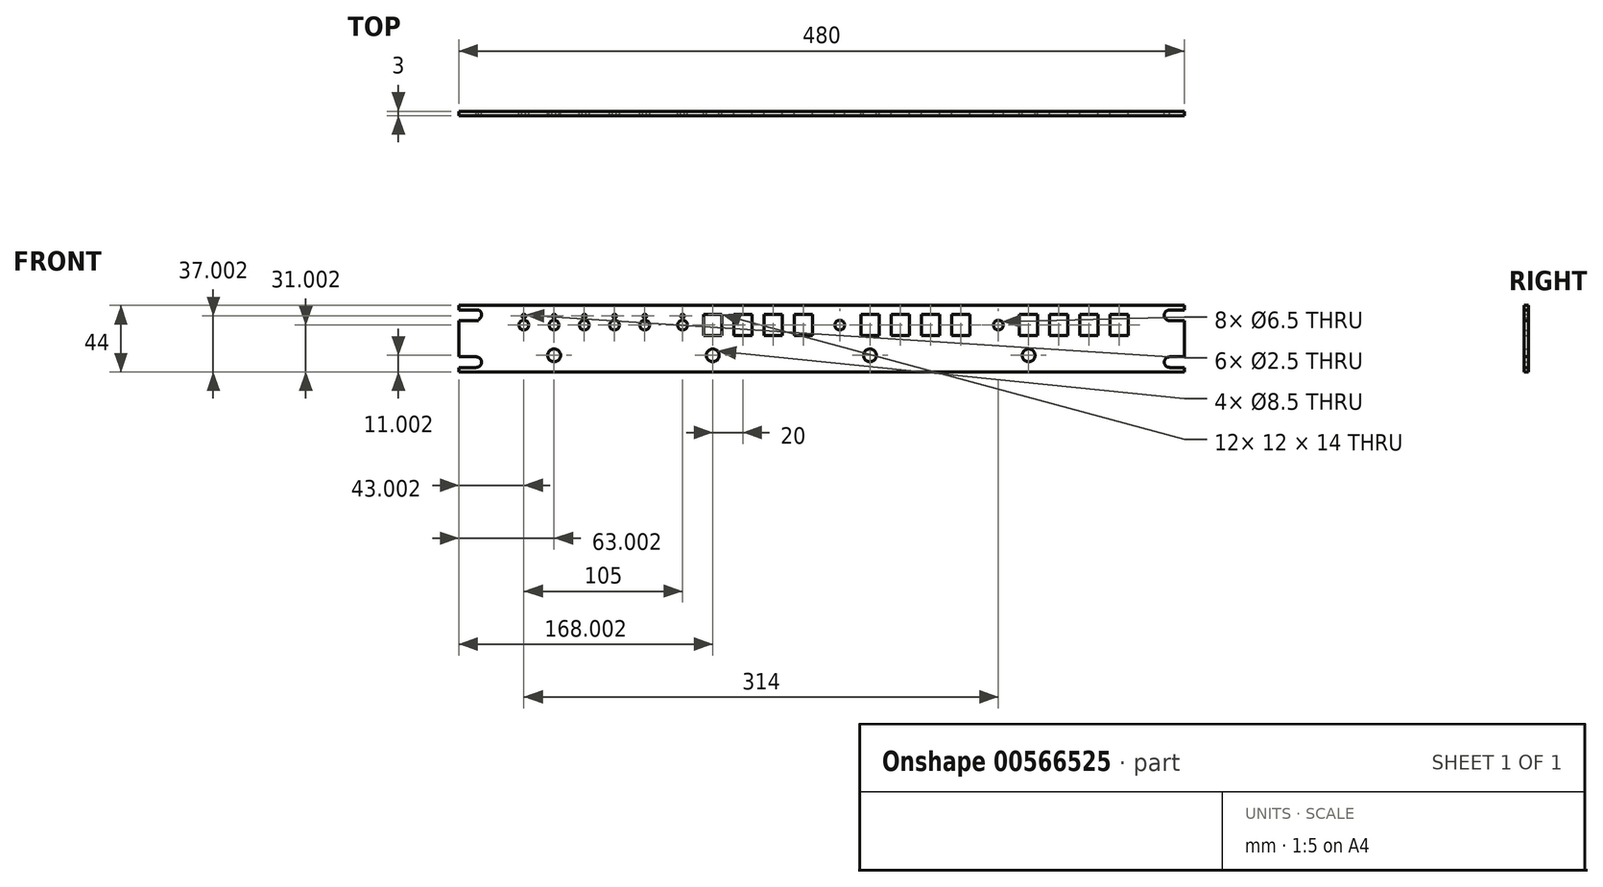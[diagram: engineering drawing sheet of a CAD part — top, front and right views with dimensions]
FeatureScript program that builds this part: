
annotation { "Feature Type Name" : "Feature", "Feature Type Description" : "" }
export const myFeature = defineFeature(function(context is Context, id is Id, definition is map)
    precondition{}
    {
        {
            var Q0;
            Q0=qCreatedBy(makeId("Front.planeOp"),FACE);
            var sketch = newSketch(context, id + "F0", { "sketchPlane" : qUnion([Q0])});
            skLineSegment(sketch, "E0.bottom", {"start": v(-244.03, -52.88) * mm, "end": v(235.97, -52.88) * mm});
            skLineSegment(sketch, "E0.top", {"start": v(-244.03, -96.88) * mm, "end": v(235.97, -96.88) * mm});
            skLineSegment(sketch, "E0.left", {"start": v(-244.03, -52.88) * mm, "end": v(-244.03, -55.88) * mm});
            skLineSegment(sketch, "E0.right", {"start": v(235.97, -52.88) * mm, "end": v(235.97, -55.88) * mm});
            skLineSegment(sketch, "E1.bottom", {"start": v(-207.03, -58.88) * mm, "end": v(-195.03, -58.88) * mm});
            skLineSegment(sketch, "E1.top", {"start": v(-207.03, -72.88) * mm, "end": v(-195.03, -72.88) * mm});
            skLineSegment(sketch, "E1.left", {"start": v(-207.03, -58.88) * mm, "end": v(-207.03, -72.88) * mm});
            skLineSegment(sketch, "E1.right", {"start": v(-195.03, -58.88) * mm, "end": v(-195.03, -72.88) * mm});
            skLineSegment(sketch, "E2.bottom", {"start": v(-187.03, -58.88) * mm, "end": v(-175.03, -58.88) * mm});
            skLineSegment(sketch, "E2.top", {"start": v(-187.03, -72.88) * mm, "end": v(-175.03, -72.88) * mm});
            skLineSegment(sketch, "E2.left", {"start": v(-187.03, -58.88) * mm, "end": v(-187.03, -72.88) * mm});
            skLineSegment(sketch, "E2.right", {"start": v(-175.03, -58.88) * mm, "end": v(-175.03, -72.88) * mm});
            skLineSegment(sketch, "E3.bottom", {"start": v(-167.03, -58.88) * mm, "end": v(-155.03, -58.88) * mm});
            skLineSegment(sketch, "E3.top", {"start": v(-167.03, -72.88) * mm, "end": v(-155.03, -72.88) * mm});
            skLineSegment(sketch, "E3.left", {"start": v(-167.03, -58.88) * mm, "end": v(-167.03, -72.88) * mm});
            skLineSegment(sketch, "E3.right", {"start": v(-155.03, -58.88) * mm, "end": v(-155.03, -72.88) * mm});
            skLineSegment(sketch, "E4.bottom", {"start": v(-147.03, -58.88) * mm, "end": v(-135.03, -58.88) * mm});
            skLineSegment(sketch, "E4.top", {"start": v(-147.03, -72.88) * mm, "end": v(-135.03, -72.88) * mm});
            skLineSegment(sketch, "E4.left", {"start": v(-147.03, -58.88) * mm, "end": v(-147.03, -72.88) * mm});
            skLineSegment(sketch, "E4.right", {"start": v(-135.03, -58.88) * mm, "end": v(-135.03, -72.88) * mm});
            skLineSegment(sketch, "E5.bottom", {"start": v(-127.03, -58.88) * mm, "end": v(-115.03, -58.88) * mm});
            skLineSegment(sketch, "E5.top", {"start": v(-127.03, -72.88) * mm, "end": v(-115.03, -72.88) * mm});
            skLineSegment(sketch, "E5.left", {"start": v(-127.03, -58.88) * mm, "end": v(-127.03, -72.88) * mm});
            skLineSegment(sketch, "E5.right", {"start": v(-115.03, -58.88) * mm, "end": v(-115.03, -72.88) * mm});
            skCircle(sketch, "E6", {"center": v(-181.03, -85.88) * mm, "radius": 4.25 * mm});
            skCircle(sketch, "E7", {"center": v(-201.03, -65.88) * mm, "radius": 3.25 * mm});
            skLineSegment(sketch, "E8.bottom", {"start": v(-102.03, -58.88) * mm, "end": v(-90.03, -58.88) * mm});
            skLineSegment(sketch, "E8.top", {"start": v(-102.03, -72.88) * mm, "end": v(-90.03, -72.88) * mm});
            skLineSegment(sketch, "E8.left", {"start": v(-102.03, -58.88) * mm, "end": v(-102.03, -72.88) * mm});
            skLineSegment(sketch, "E8.right", {"start": v(-90.03, -58.88) * mm, "end": v(-90.03, -72.88) * mm});
            skLineSegment(sketch, "E9.bottom", {"start": v(-82.03, -58.88) * mm, "end": v(-70.03, -58.88) * mm});
            skLineSegment(sketch, "E9.top", {"start": v(-82.03, -72.88) * mm, "end": v(-70.03, -72.88) * mm});
            skLineSegment(sketch, "E9.left", {"start": v(-82.03, -58.88) * mm, "end": v(-82.03, -72.88) * mm});
            skLineSegment(sketch, "E9.right", {"start": v(-70.03, -58.88) * mm, "end": v(-70.03, -72.88) * mm});
            skLineSegment(sketch, "E10.bottom", {"start": v(-62.03, -58.88) * mm, "end": v(-50.03, -58.88) * mm});
            skLineSegment(sketch, "E10.top", {"start": v(-62.03, -72.88) * mm, "end": v(-50.03, -72.88) * mm});
            skLineSegment(sketch, "E10.left", {"start": v(-62.03, -58.88) * mm, "end": v(-62.03, -72.88) * mm});
            skLineSegment(sketch, "E10.right", {"start": v(-50.03, -58.88) * mm, "end": v(-50.03, -72.88) * mm});
            skLineSegment(sketch, "E11.bottom", {"start": v(-42.03, -58.88) * mm, "end": v(-30.03, -58.88) * mm});
            skLineSegment(sketch, "E11.top", {"start": v(-42.03, -72.88) * mm, "end": v(-30.03, -72.88) * mm});
            skLineSegment(sketch, "E11.left", {"start": v(-42.03, -58.88) * mm, "end": v(-42.03, -72.88) * mm});
            skLineSegment(sketch, "E11.right", {"start": v(-30.03, -58.88) * mm, "end": v(-30.03, -72.88) * mm});
            skLineSegment(sketch, "E12.bottom", {"start": v(-22.03, -58.88) * mm, "end": v(-10.03, -58.88) * mm});
            skLineSegment(sketch, "E12.top", {"start": v(-22.03, -72.88) * mm, "end": v(-10.03, -72.88) * mm});
            skLineSegment(sketch, "E12.left", {"start": v(-22.03, -58.88) * mm, "end": v(-22.03, -72.88) * mm});
            skLineSegment(sketch, "E12.right", {"start": v(-10.03, -58.88) * mm, "end": v(-10.03, -72.88) * mm});
            skCircle(sketch, "E13", {"center": v(-76.03, -85.88) * mm, "radius": 4.25 * mm});
            skCircle(sketch, "E14", {"center": v(-96.03, -65.88) * mm, "radius": 3.25 * mm});
            skLineSegment(sketch, "E15.bottom", {"start": v(1.97, -58.88) * mm, "end": v(13.97, -58.88) * mm});
            skLineSegment(sketch, "E15.top", {"start": v(1.97, -72.88) * mm, "end": v(13.97, -72.88) * mm});
            skLineSegment(sketch, "E15.left", {"start": v(1.97, -58.88) * mm, "end": v(1.97, -72.88) * mm});
            skLineSegment(sketch, "E15.right", {"start": v(13.97, -58.88) * mm, "end": v(13.97, -72.88) * mm});
            skLineSegment(sketch, "E16.bottom", {"start": v(21.97, -58.88) * mm, "end": v(33.97, -58.88) * mm});
            skLineSegment(sketch, "E16.top", {"start": v(21.97, -72.88) * mm, "end": v(33.97, -72.88) * mm});
            skLineSegment(sketch, "E16.left", {"start": v(21.97, -58.88) * mm, "end": v(21.97, -72.88) * mm});
            skLineSegment(sketch, "E16.right", {"start": v(33.97, -58.88) * mm, "end": v(33.97, -72.88) * mm});
            skLineSegment(sketch, "E17.bottom", {"start": v(41.97, -58.88) * mm, "end": v(53.97, -58.88) * mm});
            skLineSegment(sketch, "E17.top", {"start": v(41.97, -72.88) * mm, "end": v(53.97, -72.88) * mm});
            skLineSegment(sketch, "E17.left", {"start": v(41.97, -58.88) * mm, "end": v(41.97, -72.88) * mm});
            skLineSegment(sketch, "E17.right", {"start": v(53.97, -58.88) * mm, "end": v(53.97, -72.88) * mm});
            skLineSegment(sketch, "E18.bottom", {"start": v(61.97, -58.88) * mm, "end": v(73.97, -58.88) * mm});
            skLineSegment(sketch, "E18.top", {"start": v(61.97, -72.88) * mm, "end": v(73.97, -72.88) * mm});
            skLineSegment(sketch, "E18.left", {"start": v(61.97, -58.88) * mm, "end": v(61.97, -72.88) * mm});
            skLineSegment(sketch, "E18.right", {"start": v(73.97, -58.88) * mm, "end": v(73.97, -72.88) * mm});
            skLineSegment(sketch, "E19.bottom", {"start": v(81.97, -58.88) * mm, "end": v(93.97, -58.88) * mm});
            skLineSegment(sketch, "E19.top", {"start": v(81.97, -72.88) * mm, "end": v(93.97, -72.88) * mm});
            skLineSegment(sketch, "E19.left", {"start": v(81.97, -58.88) * mm, "end": v(81.97, -72.88) * mm});
            skLineSegment(sketch, "E19.right", {"start": v(93.97, -58.88) * mm, "end": v(93.97, -72.88) * mm});
            skCircle(sketch, "E20", {"center": v(27.97, -85.88) * mm, "radius": 4.25 * mm});
            skCircle(sketch, "E21", {"center": v(7.97, -65.88) * mm, "radius": 3.25 * mm});
            skLineSegment(sketch, "E22.bottom", {"start": v(106.97, -58.88) * mm, "end": v(118.97, -58.88) * mm});
            skLineSegment(sketch, "E22.top", {"start": v(106.97, -72.88) * mm, "end": v(118.97, -72.88) * mm});
            skLineSegment(sketch, "E22.left", {"start": v(106.97, -58.88) * mm, "end": v(106.97, -72.88) * mm});
            skLineSegment(sketch, "E22.right", {"start": v(118.97, -58.88) * mm, "end": v(118.97, -72.88) * mm});
            skLineSegment(sketch, "E23.bottom", {"start": v(126.97, -58.88) * mm, "end": v(138.97, -58.88) * mm});
            skLineSegment(sketch, "E23.top", {"start": v(126.97, -72.88) * mm, "end": v(138.97, -72.88) * mm});
            skLineSegment(sketch, "E23.left", {"start": v(126.97, -58.88) * mm, "end": v(126.97, -72.88) * mm});
            skLineSegment(sketch, "E23.right", {"start": v(138.97, -58.88) * mm, "end": v(138.97, -72.88) * mm});
            skLineSegment(sketch, "E24.bottom", {"start": v(146.97, -58.88) * mm, "end": v(158.97, -58.88) * mm});
            skLineSegment(sketch, "E24.top", {"start": v(146.97, -72.88) * mm, "end": v(158.97, -72.88) * mm});
            skLineSegment(sketch, "E24.left", {"start": v(146.97, -58.88) * mm, "end": v(146.97, -72.88) * mm});
            skLineSegment(sketch, "E24.right", {"start": v(158.97, -58.88) * mm, "end": v(158.97, -72.88) * mm});
            skLineSegment(sketch, "E25.bottom", {"start": v(166.97, -58.88) * mm, "end": v(178.97, -58.88) * mm});
            skLineSegment(sketch, "E25.top", {"start": v(166.97, -72.88) * mm, "end": v(178.97, -72.88) * mm});
            skLineSegment(sketch, "E25.left", {"start": v(166.97, -58.88) * mm, "end": v(166.97, -72.88) * mm});
            skLineSegment(sketch, "E25.right", {"start": v(178.97, -58.88) * mm, "end": v(178.97, -72.88) * mm});
            skLineSegment(sketch, "E26.bottom", {"start": v(186.97, -58.88) * mm, "end": v(198.97, -58.88) * mm});
            skLineSegment(sketch, "E26.top", {"start": v(186.97, -72.88) * mm, "end": v(198.97, -72.88) * mm});
            skLineSegment(sketch, "E26.left", {"start": v(186.97, -58.88) * mm, "end": v(186.97, -72.88) * mm});
            skLineSegment(sketch, "E26.right", {"start": v(198.97, -58.88) * mm, "end": v(198.97, -72.88) * mm});
            skCircle(sketch, "E27", {"center": v(132.97, -85.88) * mm, "radius": 4.25 * mm});
            skCircle(sketch, "E28", {"center": v(112.97, -65.88) * mm, "radius": 3.25 * mm});
            skArc(sketch, "E29", {"start": v(-230.86, -62.03) * mm, "mid": v(-229.03, -58.95) * mm, "end": v(-230.86, -55.88) * mm});
            skLineSegment(sketch, "E30.bottom", {"start": v(-230.86, -55.88) * mm, "end": v(-244.03, -55.88) * mm});
            skLineSegment(sketch, "E30.top", {"start": v(-230.86, -63.01) * mm, "end": v(-244.03, -63.01) * mm});
            skLineSegment(sketch, "E30.left", {"start": v(-230.86, -62.03) * mm, "end": v(-230.86, -63.01) * mm});
            skLineSegment(sketch, "E31.trimOffspring", {"start": v(-244.03, -63.01) * mm, "end": v(-244.03, -86.88) * mm});
            skArc(sketch, "E32", {"start": v(-232.6, -93.88) * mm, "mid": v(-229.03, -90.38) * mm, "end": v(-232.6, -86.88) * mm});
            skLineSegment(sketch, "E33.bottom", {"start": v(-232.6, -86.88) * mm, "end": v(-244.03, -86.88) * mm});
            skLineSegment(sketch, "E33.top", {"start": v(-232.6, -93.88) * mm, "end": v(-244.03, -93.88) * mm});
            skLineSegment(sketch, "E33.left", {"start": v(-232.6, -93.88) * mm, "end": v(-232.6, -93.88) * mm});
            skLineSegment(sketch, "E34.trimOffspring", {"start": v(-244.03, -93.88) * mm, "end": v(-244.03, -96.88) * mm});
            skLineSegment(sketch, "E35.MirrorCS", {"start": v(226.3, -93.88) * mm, "end": v(226.3, -93.88) * mm});
            skLineSegment(sketch, "E36.MirrorCS", {"start": v(226.3, -62.88) * mm, "end": v(226.3, -63.01) * mm});
            skLineSegment(sketch, "E37.MirrorCS", {"start": v(226.3, -55.88) * mm, "end": v(235.97, -55.88) * mm});
            skArc(sketch, "E38.MirrorCS", {"start": v(226.3, -62.88) * mm, "mid": v(222.72, -59.38) * mm, "end": v(226.3, -55.88) * mm});
            skArc(sketch, "E39.MirrorCS", {"start": v(226.3, -93.88) * mm, "mid": v(222.72, -90.38) * mm, "end": v(226.3, -86.88) * mm});
            skLineSegment(sketch, "E40.MirrorCS", {"start": v(226.3, -93.88) * mm, "end": v(235.97, -93.88) * mm});
            skLineSegment(sketch, "E41.MirrorCS", {"start": v(226.3, -63.01) * mm, "end": v(235.97, -63.01) * mm});
            skLineSegment(sketch, "E42.MirrorCS", {"start": v(226.3, -86.88) * mm, "end": v(235.97, -86.88) * mm});
            skPoint(sketch, "E43.left.end.orphan", {"position": v(250.46, -53.67) * mm});
            skLineSegment(sketch, "E44.trimOffspring", {"start": v(235.97, -93.88) * mm, "end": v(235.97, -96.88) * mm});
            skLineSegment(sketch, "E45.trimOffspring", {"start": v(235.97, -63.01) * mm, "end": v(235.97, -86.88) * mm});
            skCircle(sketch, "E46", {"center": v(-181.03, -65.88) * mm, "radius": 3.25 * mm});
            skCircle(sketch, "E47", {"center": v(-121.03, -65.88) * mm, "radius": 3.25 * mm});
            skPoint(sketch, "E47.centerSnap0", {"position": v(-127.03, -65.88) * mm});
            skCircle(sketch, "E48", {"center": v(-161.03, -65.88) * mm, "radius": 3.25 * mm});
            skCircle(sketch, "E49", {"center": v(-141.03, -65.88) * mm, "radius": 3.25 * mm});
            skCircle(sketch, "E50", {"center": v(-201.03, -59.88) * mm, "radius": 1.25 * mm});
            skPoint(sketch, "E50.centerSnap0", {"position": v(-201.03, -58.88) * mm});
            skCircle(sketch, "E51", {"center": v(-181.03, -59.88) * mm, "radius": 1.25 * mm});
            skCircle(sketch, "E52", {"center": v(-161.03, -59.88) * mm, "radius": 1.25 * mm});
            skCircle(sketch, "E53", {"center": v(-141.03, -59.88) * mm, "radius": 1.25 * mm});
            skCircle(sketch, "E54", {"center": v(-121.03, -59.88) * mm, "radius": 1.25 * mm});
            skCircle(sketch, "E55", {"center": v(-96.03, -59.88) * mm, "radius": 1.25 * mm});
            skSolve(sketch);
        }
        {
            var Q0;
            Q0 = qSketchRegion(id + "F0", true);
            var Q1;
            Q1=makeQuery(id+"F0.imprint","IMPRINT",FACE,{"disambiguationData":[TD([[makeQuery(id+"F0.imprint","IMPRINT",EDGE,{"derivedFrom":sQuery(id+"F0.wireOp",EDGE,"E1.bottom")}),-1.0]])]});
            var Q2;
            Q2=makeQuery(id+"F0.imprint","IMPRINT",FACE,{"disambiguationData":[TD([[makeQuery(id+"F0.imprint","IMPRINT",EDGE,{"derivedFrom":sQuery(id+"F0.wireOp",EDGE,"E2.bottom")}),-1.0]])]});
            var Q3;
            Q3=makeQuery(id+"F0.imprint","IMPRINT",FACE,{"disambiguationData":[TD([[makeQuery(id+"F0.imprint","IMPRINT",EDGE,{"derivedFrom":sQuery(id+"F0.wireOp",EDGE,"E5.bottom")}),-1.0]])]});
            var Q4;
            Q4=makeQuery(id+"F0.imprint","IMPRINT",FACE,{"disambiguationData":[TD([[makeQuery(id+"F0.imprint","IMPRINT",EDGE,{"derivedFrom":sQuery(id+"F0.wireOp",EDGE,"E8.bottom")}),-1.0]])]});
            var Q5;
            Q5=makeQuery(id+"F0.imprint","IMPRINT",FACE,{"disambiguationData":[TD([[makeQuery(id+"F0.imprint","IMPRINT",EDGE,{"derivedFrom":sQuery(id+"F0.wireOp",EDGE,"E15.bottom")}),-1.0]])]});
            var Q6;
            Q6=makeQuery(id+"F0.imprint","IMPRINT",FACE,{"disambiguationData":[TD([[makeQuery(id+"F0.imprint","IMPRINT",EDGE,{"derivedFrom":sQuery(id+"F0.wireOp",EDGE,"E22.bottom")}),-1.0]])]});
            var Q7;
            Q7=makeQuery(id+"F0.imprint","IMPRINT",FACE,{"disambiguationData":[TD([[makeQuery(id+"F0.imprint","IMPRINT",EDGE,{"derivedFrom":sQuery(id+"F0.wireOp",EDGE,"E3.bottom")}),-1.0]])]});
            var Q8;
            Q8=makeQuery(id+"F0.imprint","IMPRINT",FACE,{"disambiguationData":[TD([[makeQuery(id+"F0.imprint","IMPRINT",EDGE,{"derivedFrom":sQuery(id+"F0.wireOp",EDGE,"E4.bottom")}),-1.0]])]});
            extrude(context, id + "F1", {"entities" : qUnion([Q0, Q1, Q2, Q3, Q4, Q5, Q6, Q7, Q8]), "depth" : 3 * mm, "offsetDistance" : 25 * mm});
        }
    });
